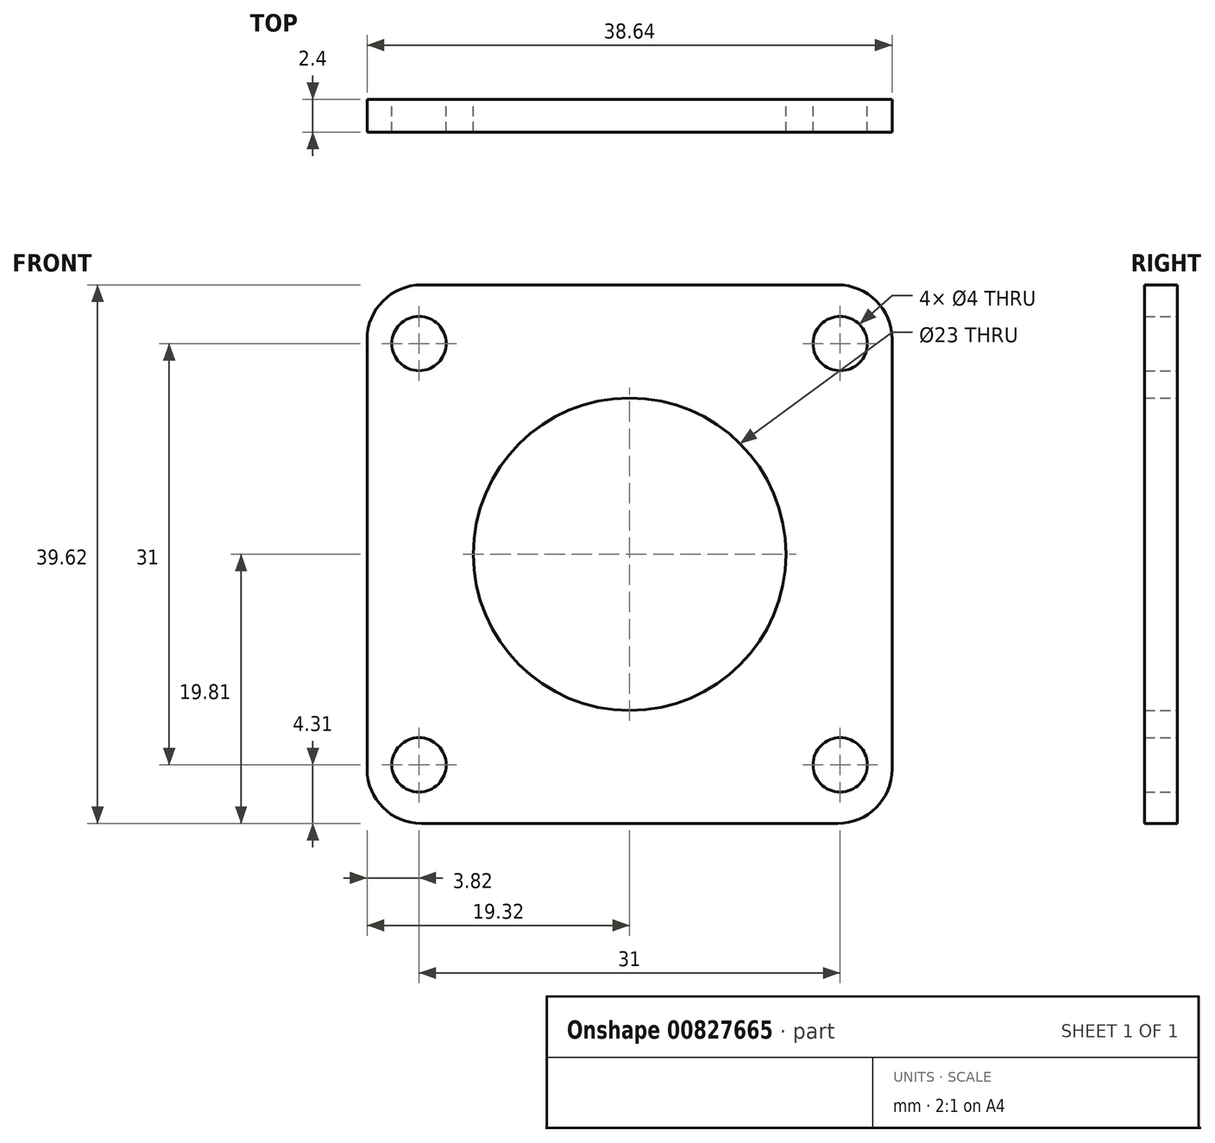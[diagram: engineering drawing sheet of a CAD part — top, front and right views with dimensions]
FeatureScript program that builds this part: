
annotation { "Feature Type Name" : "Feature", "Feature Type Description" : "" }
export const myFeature = defineFeature(function(context is Context, id is Id, definition is map)
    precondition{}
    {
        {
            var Q0;
            Q0=qCreatedBy(makeId("Front.planeOp"),FACE);
            var sketch = newSketch(context, id + "F0", { "sketchPlane" : qUnion([Q0])});
            skLineSegment(sketch, "E0.bottom", {"start": v(-15.5, 15.5) * mm, "end": v(15.5, 15.5) * mm, "construction": true});
            skLineSegment(sketch, "E0.top", {"start": v(-15.5, -15.5) * mm, "end": v(15.5, -15.5) * mm, "construction": true});
            skLineSegment(sketch, "E0.left", {"start": v(-15.5, 15.5) * mm, "end": v(-15.5, -15.5) * mm, "construction": true});
            skLineSegment(sketch, "E0.right", {"start": v(15.5, 15.5) * mm, "end": v(15.5, -15.5) * mm, "construction": true});
            skPoint(sketch, "E0.middle", {"position": v(0, 0) * mm});
            skCircle(sketch, "E1", {"center": v(-15.5, 15.5) * mm, "radius": 2 * mm});
            skCircle(sketch, "E2", {"center": v(15.5, 15.5) * mm, "radius": 2 * mm});
            skCircle(sketch, "E3", {"center": v(15.5, -15.5) * mm, "radius": 2 * mm});
            skCircle(sketch, "E4", {"center": v(-15.5, -15.5) * mm, "radius": 2 * mm});
            skCircle(sketch, "E5", {"center": v(0, 0) * mm, "radius": 11.5 * mm});
            skLineSegment(sketch, "E6", {"start": v(-17.5, 15.5) * mm, "end": v(-17.5, -15.5) * mm});
            skLineSegment(sketch, "E7", {"start": v(-15.5, -17.5) * mm, "end": v(15.5, -17.5) * mm});
            skLineSegment(sketch, "E8", {"start": v(17.5, -15.5) * mm, "end": v(17.5, 15.5) * mm});
            skLineSegment(sketch, "E9", {"start": v(15.5, 17.5) * mm, "end": v(-15.5, 17.5) * mm});
            skLineSegment(sketch, "E10.bottom", {"start": v(-15.32, 19.81) * mm, "end": v(15.32, 19.81) * mm});
            skLineSegment(sketch, "E10.top", {"start": v(-15.32, -19.81) * mm, "end": v(15.32, -19.81) * mm});
            skLineSegment(sketch, "E10.left", {"start": v(-19.32, 15.81) * mm, "end": v(-19.32, -15.81) * mm});
            skLineSegment(sketch, "E10.right", {"start": v(19.32, 15.81) * mm, "end": v(19.32, -15.81) * mm});
            skPoint(sketch, "E11.visualSharp", {"position": v(-19.32, 19.81) * mm});
            skArc(sketch, "E11.filletArc", {"start": v(-15.32, 19.81) * mm, "mid": v(-18.15, 18.64) * mm, "end": v(-19.32, 15.81) * mm});
            skPoint(sketch, "E12.visualSharp", {"position": v(19.32, 19.81) * mm});
            skArc(sketch, "E12.filletArc", {"start": v(19.32, 15.81) * mm, "mid": v(18.15, 18.64) * mm, "end": v(15.32, 19.81) * mm});
            skPoint(sketch, "E13.visualSharp", {"position": v(19.32, -19.81) * mm});
            skArc(sketch, "E13.filletArc", {"start": v(15.32, -19.81) * mm, "mid": v(18.15, -18.64) * mm, "end": v(19.32, -15.81) * mm});
            skPoint(sketch, "E14.visualSharp", {"position": v(-19.32, -19.81) * mm});
            skArc(sketch, "E14.filletArc", {"start": v(-19.32, -15.81) * mm, "mid": v(-18.15, -18.64) * mm, "end": v(-15.32, -19.81) * mm});
            skSolve(sketch);
        }
        {
            var Q0;
            Q0=makeQuery(id+"F0.imprint","IMPRINT",FACE,{"disambiguationData":[TD([[makeQuery(id+"F0.imprint","IMPRINT",EDGE,{"derivedFrom":sQuery(id+"F0.wireOp",EDGE,"E5")}),-1.0]])]});
            var Q1;
            {var subQ2=sQuery(id+"F0.wireOp",EDGE,"E6");Q1=makeQuery(id+"F0.imprint","IMPRINT",FACE,{"disambiguationData":[TD([[makeQuery(id+"F0.imprint","IMPRINT",EDGE,{"derivedFrom":subQ2}),-1.0]])]});}
            extrude(context, id + "F1", {"entities" : qUnion([Q0, Q1]), "depth" : 2.4 * mm, "offsetDistance" : 25 * mm});
        }
    });
